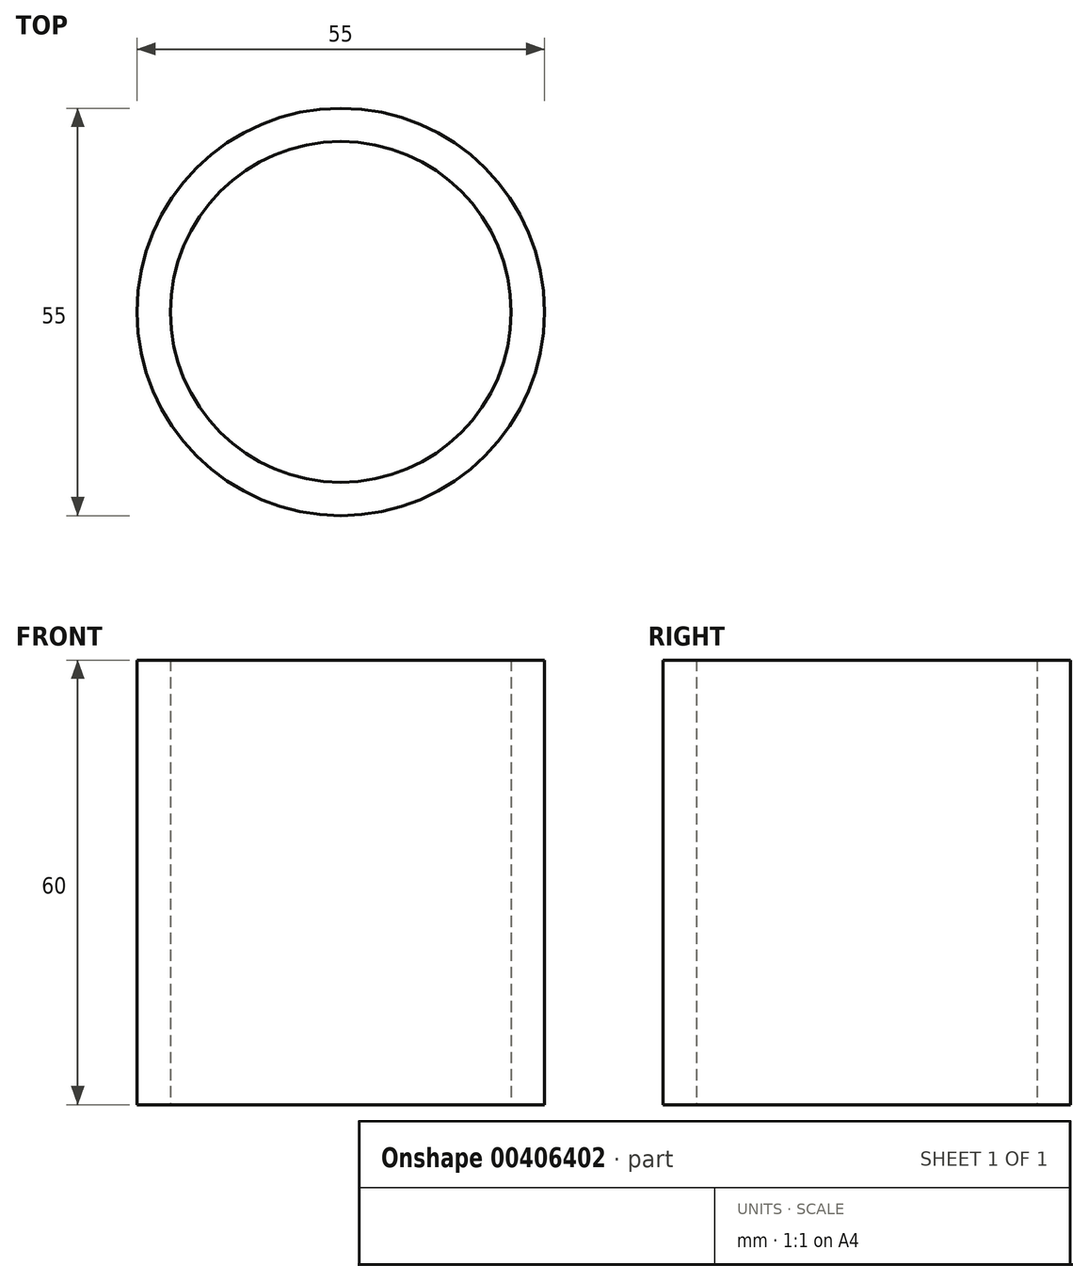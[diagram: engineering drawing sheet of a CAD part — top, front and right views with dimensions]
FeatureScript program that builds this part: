
annotation { "Feature Type Name" : "Feature", "Feature Type Description" : "" }
export const myFeature = defineFeature(function(context is Context, id is Id, definition is map)
    precondition{}
    {
        {
            var Q0;
            Q0=qCreatedBy(makeId("Top.planeOp"),FACE);
            var sketch = newSketch(context, id + "F0", { "sketchPlane" : qUnion([Q0])});
            skCircle(sketch, "E0", {"center": v(0, 0) * mm, "radius": 23 * mm});
            skCircle(sketch, "E1", {"center": v(9.4, 9.5) * mm, "radius": 9.5 * mm, "construction": true});
            skCircle(sketch, "E2", {"center": v(9.4, -9.5) * mm, "radius": 9.5 * mm, "construction": true});
            skCircle(sketch, "E3", {"center": v(-9.6, -9.5) * mm, "radius": 9.5 * mm, "construction": true});
            skCircle(sketch, "E4", {"center": v(-9.6, 9.5) * mm, "radius": 9.5 * mm, "construction": true});
            skCircle(sketch, "E5", {"center": v(0, 0) * mm, "radius": 27.5 * mm});
            skSolve(sketch);
        }
        {
            var Q0;
            Q0=makeQuery(id+"F0.imprint","IMPRINT",FACE,{"disambiguationData":[TD([[makeQuery(id+"F0.imprint","IMPRINT",EDGE,{"derivedFrom":sQuery(id+"F0.wireOp",EDGE,"E0")}),-1.0]])]});
            extrude(context, id + "F1", {"entities" : qUnion([Q0]), "depth" : 60 * mm, "offsetDistance" : 25 * mm});
        }
    });
